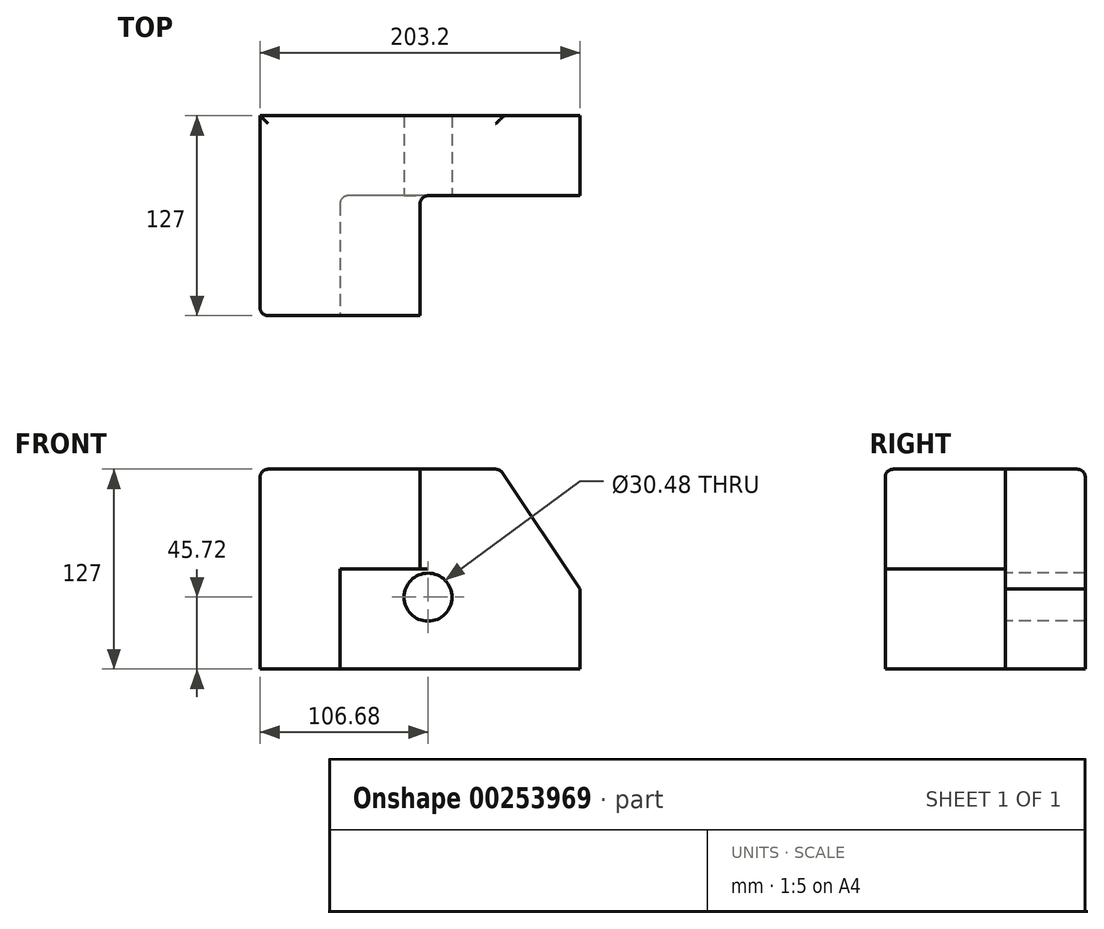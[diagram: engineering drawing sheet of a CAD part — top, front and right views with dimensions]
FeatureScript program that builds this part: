
annotation { "Feature Type Name" : "Feature", "Feature Type Description" : "" }
export const myFeature = defineFeature(function(context is Context, id is Id, definition is map)
    precondition{}
    {
        {
            var Q0;
            Q0=qCreatedBy(makeId("Front.planeOp"),FACE);
            var sketch = newSketch(context, id + "F0", { "sketchPlane" : qUnion([Q0])});
            skLineSegment(sketch, "E0.bottom", {"start": v(101.6, -63.5) * mm, "end": v(-101.6, -63.5) * mm});
            skLineSegment(sketch, "E0.top", {"start": v(101.6, 63.5) * mm, "end": v(-101.6, 63.5) * mm});
            skLineSegment(sketch, "E0.left", {"start": v(101.6, -63.5) * mm, "end": v(101.6, 63.5) * mm});
            skLineSegment(sketch, "E0.right", {"start": v(-101.6, -63.5) * mm, "end": v(-101.6, 63.5) * mm});
            skPoint(sketch, "E0.middle", {"position": v(0, 0) * mm});
            skSolve(sketch);
        }
        {
            var Q0;
            Q0 = qSketchRegion(id + "F0", true);
            extrude(context, id + "F1", {"entities" : qUnion([Q0]), "depth" : 127 * mm});
        }
        {
            var Q0;
            Q0=makeQuery(id+"F1.opExtrude","CAP_FACE",FACE,{"disambiguationData":[OSD([sQuery(id+"F0.wireOp",EDGE,"E0.bottom"),sQuery(id+"F0.wireOp",EDGE,"E0.top"),sQuery(id+"F0.wireOp",EDGE,"E0.left"),sQuery(id+"F0.wireOp",EDGE,"E0.right")])],"isStart":false});
            var sketch = newSketch(context, id + "F2", { "sketchPlane" : qUnion([Q0])});
            skLineSegment(sketch, "E1", {"start": v(0, 63.5) * mm, "end": v(0, 0) * mm});
            skLineSegment(sketch, "E2", {"start": v(0, 0) * mm, "end": v(-50.8, 0) * mm});
            skLineSegment(sketch, "E3", {"start": v(-50.8, 0) * mm, "end": v(-50.8, -63.5) * mm});
            skSolve(sketch);
        }
        {
            var Q0;
            Q0 = qSketchRegion(id + "F2", true);
            var Q1;
            {var subQ2=sQuery(id+"F2.wireOp",EDGE,"E1");Q1=makeQuery(id+"F2.imprint","IMPRINT",FACE,{"disambiguationData":[TD([[makeQuery(id+"F2.imprint","IMPRINT",EDGE,{"derivedFrom":subQ2}),1.0]])]});}
            extrude(context, id + "F3", {"entities" : qUnion([Q0, Q1]), "operationType" : NewBodyOperationType.REMOVE, "oppositeDirection" : true, "depth" : 76.2 * mm});
        }
        {
            var Q0;
            Q0=makeQuery(id+"F1.opExtrude","SWEPT_EDGE",EDGE,{"disambiguationData":[OSD([sQuery(id+"F0.wireOp",EDGE,"E0.top"),sQuery(id+"F0.wireOp",EDGE,"E0.left")])]});
            chamfer(context, id + "F4", {"entities" : qUnion([Q0]), "chamferType" : ChamferType.TWO_OFFSETS, "width1" : 50.8 * mm, "oppositeDirection" : false, "width2" : 76.2 * mm, "tangentPropagation" : true});
        }
        {
            var Q0;
            Q0=makeQuery(id+"F3.boolean.opBoolean","COPY",EDGE,{"derivedFrom":makeQuery(id+"F3.opExtrude","CAP_EDGE",EDGE,{"disambiguationData":[OSD([sQuery(id+"F0.wireOp",EDGE,"E0.top")])],"isStart":false})});
            var Q1;
            Q1=makeQuery(id+"F1.opExtrude","CAP_EDGE",EDGE,{"disambiguationData":[OSD([sQuery(id+"F0.wireOp",EDGE,"E0.top")])],"isStart":true});
            var Q2;
            {var subQ0=sQuery(id+"F0.wireOp",EDGE,"E0.top");Q2=makeQuery(id+"F4.opChamfer","BLEND_EDGE",EDGE,{"blendedFrom":[makeQuery(id+"F1.opExtrude","SWEPT_EDGE",EDGE,{"disambiguationData":[OSD([subQ0,sQuery(id+"F0.wireOp",EDGE,"E0.left")])]}),makeQuery(id+"F1.opExtrude","SWEPT_FACE",FACE,{"disambiguationData":[OSD([subQ0])]})],"blendedInto":[makeQuery(id+"F1.opExtrude","SWEPT_FACE",FACE,{"disambiguationData":[OSD([subQ0])]})]});}
            var Q3;
            Q3=makeQuery(id+"F1.opExtrude","SWEPT_EDGE",EDGE,{"disambiguationData":[OSD([sQuery(id+"F0.wireOp",EDGE,"E0.top"),sQuery(id+"F0.wireOp",EDGE,"E0.right")])]});
            var Q4;
            Q4=makeQuery(id+"F1.opExtrude","CAP_EDGE",EDGE,{"disambiguationData":[OSD([sQuery(id+"F0.wireOp",EDGE,"E0.top")])],"isStart":false});
            var Q5;
            Q5=makeQuery(id+"F3.boolean.opBoolean","COPY",EDGE,{"derivedFrom":makeQuery(id+"F3.opExtrude","SWEPT_EDGE",EDGE,{"disambiguationData":[OSD([sQuery(id+"F0.wireOp",EDGE,"E0.top"),sQuery(id+"F2.wireOp",EDGE,"E1")])]})});
            var Q6;
            Q6=makeQuery(id+"F3.boolean.opBoolean","COPY",EDGE,{"derivedFrom":makeQuery(id+"F3.opExtrude","CAP_EDGE",EDGE,{"disambiguationData":[OSD([sQuery(id+"F2.wireOp",EDGE,"E1")])],"isStart":true})});
            var Q7;
            Q7=makeQuery(id+"F3.boolean.opBoolean","COPY",EDGE,{"derivedFrom":makeQuery(id+"F3.opExtrude","CAP_EDGE",EDGE,{"disambiguationData":[OSD([sQuery(id+"F2.wireOp",EDGE,"E1")])],"isStart":false})});
            var Q8;
            Q8=makeQuery(id+"F3.boolean.opBoolean","COPY",EDGE,{"derivedFrom":makeQuery(id+"F3.opExtrude","SWEPT_EDGE",EDGE,{"disambiguationData":[OSD([sQuery(id+"F0.wireOp",EDGE,"E0.bottom"),sQuery(id+"F2.wireOp",EDGE,"E3")])]})});
            var Q9;
            Q9=makeQuery(id+"F3.boolean.opBoolean","COPY",EDGE,{"derivedFrom":makeQuery(id+"F3.opExtrude","CAP_EDGE",EDGE,{"disambiguationData":[OSD([sQuery(id+"F0.wireOp",EDGE,"E0.bottom")])],"isStart":false})});
            var Q10;
            Q10=makeQuery(id+"F3.boolean.opBoolean","COPY",EDGE,{"derivedFrom":makeQuery(id+"F3.opExtrude","CAP_EDGE",EDGE,{"disambiguationData":[OSD([sQuery(id+"F2.wireOp",EDGE,"E3")])],"isStart":false})});
            var Q11;
            Q11=makeQuery(id+"F3.boolean.opBoolean","COPY",EDGE,{"derivedFrom":makeQuery(id+"F3.opExtrude","CAP_EDGE",EDGE,{"disambiguationData":[OSD([sQuery(id+"F2.wireOp",EDGE,"E3")])],"isStart":true})});
            var Q12;
            Q12=makeQuery(id+"F3.boolean.opBoolean","COPY",EDGE,{"derivedFrom":makeQuery(id+"F3.opExtrude","CAP_EDGE",EDGE,{"disambiguationData":[OSD([sQuery(id+"F2.wireOp",EDGE,"E2")])],"isStart":true})});
            var Q13;
            Q13=makeQuery(id+"F1.opExtrude","CAP_EDGE",EDGE,{"disambiguationData":[OSD([sQuery(id+"F0.wireOp",EDGE,"E0.right")])],"isStart":false});
            fillet(context, id + "F5", {"entities" : qUnion([Q0, Q1, Q2, Q3, Q4, Q5, Q6, Q7, Q8, Q9, Q10, Q11, Q12, Q13]), "radius" : 5.08 * mm, "tangentPropagation" : true, "allowEdgeOverflow" : false});
        }
        {
            var Q0;
            Q0=makeQuery(id+"F3.boolean.opBoolean","COPY",FACE,{"derivedFrom":makeQuery(id+"F3.opExtrude","CAP_FACE",FACE,{"disambiguationData":[OSD([sQuery(id+"F0.wireOp",EDGE,"E0.bottom"),sQuery(id+"F0.wireOp",EDGE,"E0.top"),sQuery(id+"F0.wireOp",EDGE,"E0.left"),sQuery(id+"F2.wireOp",EDGE,"E1"),sQuery(id+"F2.wireOp",EDGE,"E2"),sQuery(id+"F2.wireOp",EDGE,"E3")])],"isStart":false})});
            var sketch = newSketch(context, id + "F6", { "sketchPlane" : qUnion([Q0])});
            skCircle(sketch, "E4", {"center": v(5.08, -17.78) * mm, "radius": 15.24 * mm});
            skSolve(sketch);
        }
        {
            var Q0;
            Q0=makeQuery(id+"F6.imprint","IMPRINT",FACE,{"disambiguationData":[TD([[makeQuery(id+"F6.imprint","IMPRINT",EDGE,{"derivedFrom":sQuery(id+"F6.wireOp",EDGE,"E4")}),1.0]])]});
            var Q1;
            Q1=makeQuery(id+"F1.opExtrude","CAP_FACE",FACE,{"disambiguationData":[OSD([sQuery(id+"F0.wireOp",EDGE,"E0.bottom"),sQuery(id+"F0.wireOp",EDGE,"E0.top"),sQuery(id+"F0.wireOp",EDGE,"E0.left"),sQuery(id+"F0.wireOp",EDGE,"E0.right")])],"isStart":true});
            extrude(context, id + "F7", {"entities" : qUnion([Q0]), "operationType" : NewBodyOperationType.REMOVE, "endBound" : BoundingType.UP_TO_SURFACE, "oppositeDirection" : true, "endBoundEntityFace" : qUnion([Q1]), "depth" : 25.4 * mm});
        }
    });
